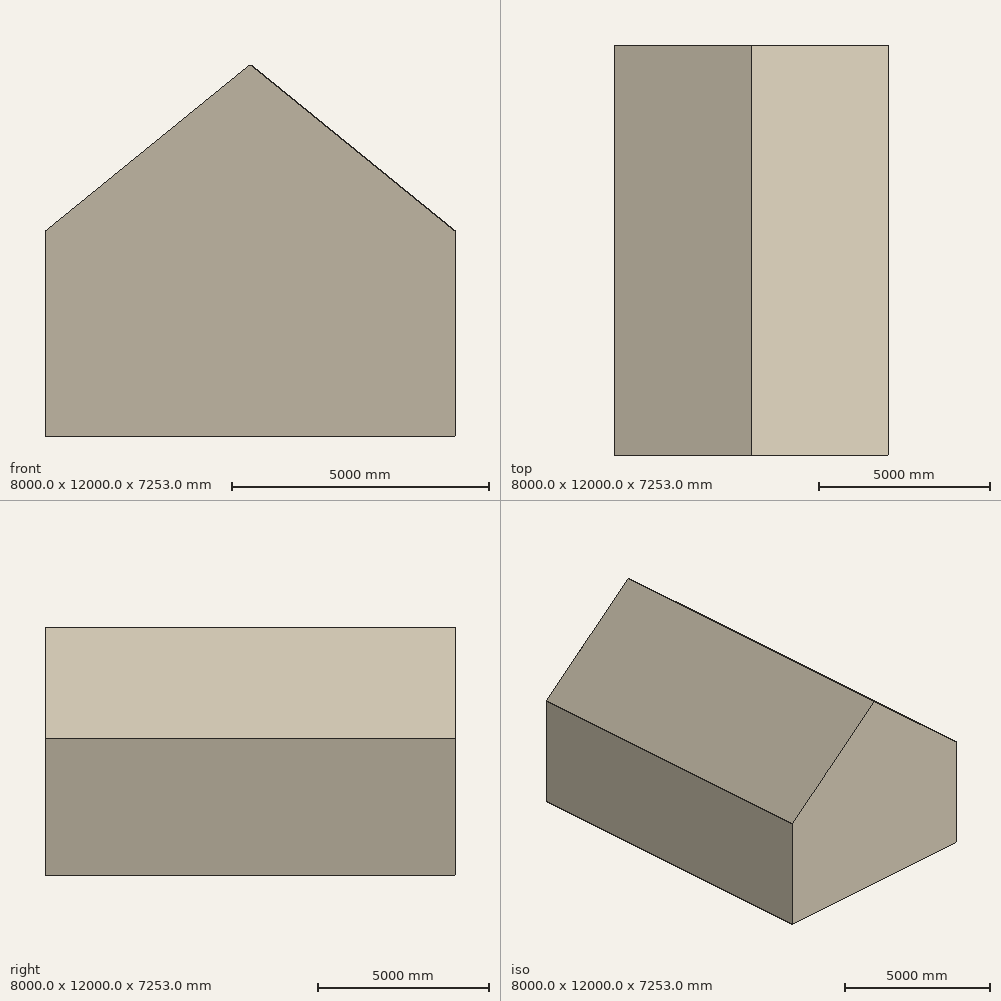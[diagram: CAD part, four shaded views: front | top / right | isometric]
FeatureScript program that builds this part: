
annotation { "Feature Type Name" : "Feature", "Feature Type Description" : "" }
export const myFeature = defineFeature(function(context is Context, id is Id, definition is map)
    precondition{}
    {
        {
            var Q0;
            Q0=qCreatedBy(makeId("Front.planeOp"),FACE);
            var sketch = newSketch(context, id + "F0", { "sketchPlane" : qUnion([Q0])});
            skLineSegment(sketch, "E0", {"start": v(-8000, 0) * mm, "end": v(-8000, -4000) * mm});
            skLineSegment(sketch, "E1", {"start": v(-8000, -4000) * mm, "end": v(0, -4000) * mm});
            skLineSegment(sketch, "E2", {"start": v(0, -4000) * mm, "end": v(0, 0) * mm});
            skLineSegment(sketch, "E3", {"start": v(0, 0) * mm, "end": v(-4000, 3253.03) * mm});
            skLineSegment(sketch, "E4", {"start": v(-4000, 3253.03) * mm, "end": v(-8000, 0) * mm});
            skSolve(sketch);
        }
        {
            var Q0;
            Q0 = qSketchRegion(id + "F0", true);
            extrude(context, id + "F1", {"entities" : qUnion([Q0]), "depth" : 12000 * mm});
        }
    });
